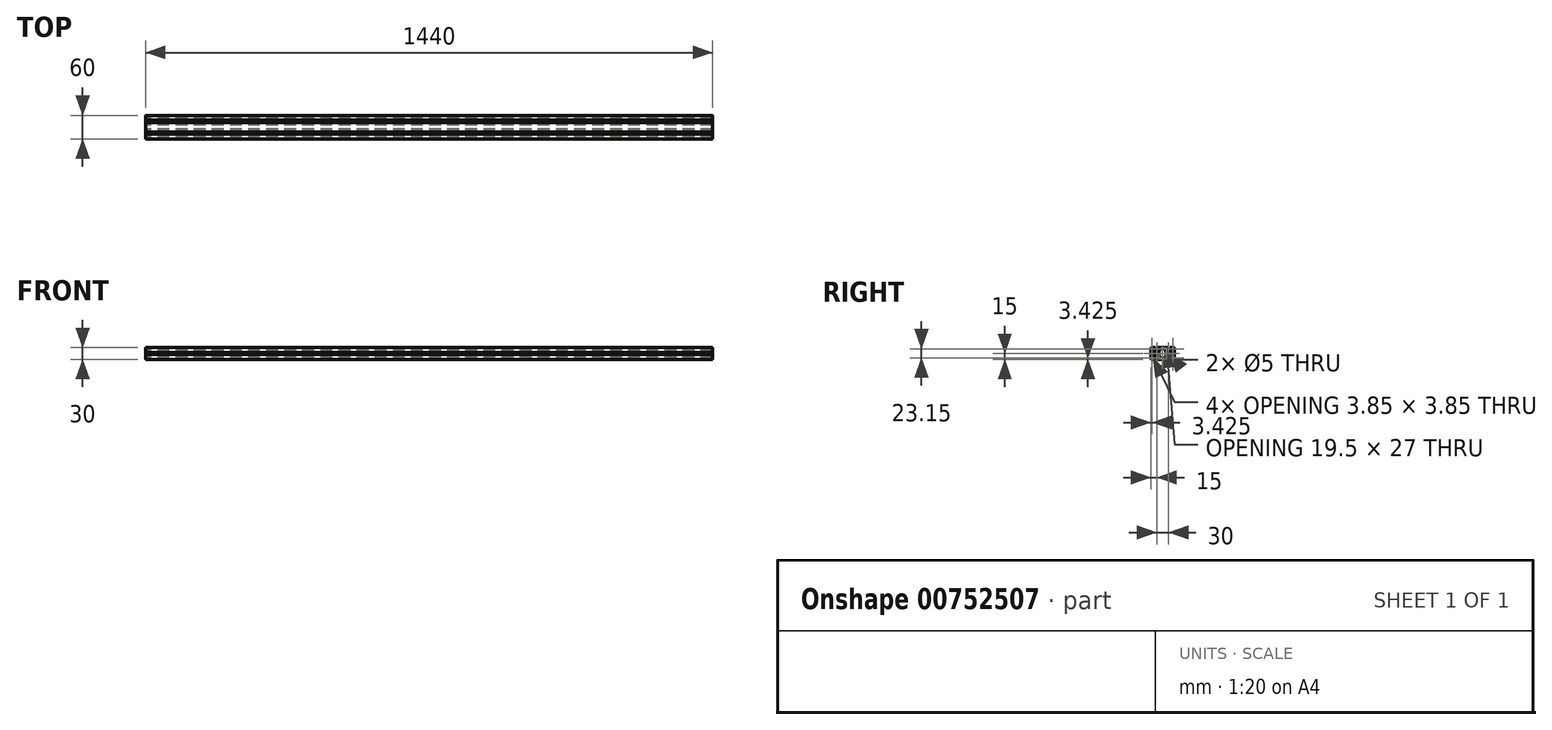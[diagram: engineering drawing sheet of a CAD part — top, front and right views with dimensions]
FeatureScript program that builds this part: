
annotation { "Feature Type Name" : "Feature", "Feature Type Description" : "" }
export const myFeature = defineFeature(function(context is Context, id is Id, definition is map)
    precondition{}
    {
        {
            var Q0;
            Q0=qCreatedBy(makeId("Right.planeOp"),FACE);
            var sketch = newSketch(context, id + "F0", { "sketchPlane" : qUnion([Q0])});
            skLineSegment(sketch, "E0.bottom", {"start": v(-12, 15) * mm, "end": v(-3.1, 15) * mm});
            skLineSegment(sketch, "E0.top", {"start": v(-12, -15) * mm, "end": v(-3.1, -15) * mm});
            skLineSegment(sketch, "E1", {"start": v(0, 31.7) * mm, "end": v(0, -24.01) * mm, "construction": true});
            skLineSegment(sketch, "E2", {"start": v(-29.71, 0) * mm, "end": v(21.95, 0) * mm, "construction": true});
            skLineSegment(sketch, "E3", {"start": v(-3.1, 15) * mm, "end": v(-3.1, 12.8) * mm});
            skLineSegment(sketch, "E4", {"start": v(-3.9, 12) * mm, "end": v(-5.6, 12) * mm});
            skLineSegment(sketch, "E5", {"start": v(-5.6, 12) * mm, "end": v(-5.6, 13.5) * mm});
            skLineSegment(sketch, "E6", {"start": v(-5.6, 13.5) * mm, "end": v(-8.15, 13.5) * mm});
            skLineSegment(sketch, "E7", {"start": v(-8.15, 13.5) * mm, "end": v(-8.15, 10.8) * mm});
            skLineSegment(sketch, "E8", {"start": v(-7.27, 8.68) * mm, "end": v(-4.72, 6.13) * mm});
            skLineSegment(sketch, "E9", {"start": v(-2.6, 5.25) * mm, "end": v(2.6, 5.25) * mm});
            skLineSegment(sketch, "E10", {"start": v(4.72, 6.13) * mm, "end": v(7.27, 8.68) * mm});
            skLineSegment(sketch, "E11", {"start": v(8.15, 10.8) * mm, "end": v(8.15, 13.5) * mm});
            skLineSegment(sketch, "E12", {"start": v(8.15, 13.5) * mm, "end": v(5.6, 13.5) * mm});
            skLineSegment(sketch, "E13", {"start": v(5.6, 13.5) * mm, "end": v(5.6, 12) * mm});
            skLineSegment(sketch, "E14", {"start": v(5.6, 12) * mm, "end": v(3.9, 12) * mm});
            skLineSegment(sketch, "E15", {"start": v(3.1, 12.8) * mm, "end": v(3.1, 15) * mm});
            skLineSegment(sketch, "E16.trimOffspring", {"start": v(3.1, 15) * mm, "end": v(12, 15) * mm});
            skLineSegment(sketch, "E17.bottom", {"start": v(-12, 13.5) * mm, "end": v(-9.65, 13.5) * mm});
            skLineSegment(sketch, "E17.top", {"start": v(-13.5, 9.65) * mm, "end": v(-9.65, 9.65) * mm});
            skLineSegment(sketch, "E17.left", {"start": v(-13.5, 12) * mm, "end": v(-13.5, 9.65) * mm});
            skLineSegment(sketch, "E17.right", {"start": v(-9.65, 13.5) * mm, "end": v(-9.65, 9.65) * mm});
            skPoint(sketch, "E18.visualSharp", {"position": v(-13.5, 13.5) * mm});
            skArc(sketch, "E18.filletArc", {"start": v(-12, 13.5) * mm, "mid": v(-13.06, 13.06) * mm, "end": v(-13.5, 12) * mm});
            skPoint(sketch, "E19.visualSharp", {"position": v(-14.85, 15) * mm});
            skArc(sketch, "E19.filletArc", {"start": v(-12, 15) * mm, "mid": v(-14.12, 14.12) * mm, "end": v(-15, 12) * mm});
            skPoint(sketch, "E20.visualSharp", {"position": v(-14.85, -15) * mm});
            skArc(sketch, "E20.filletArc", {"start": v(-15, -12) * mm, "mid": v(-14.12, -14.12) * mm, "end": v(-12, -15) * mm});
            skPoint(sketch, "E21.visualSharp", {"position": v(15.15, -15) * mm});
            skPoint(sketch, "E22.visualSharp", {"position": v(-8.15, 9.56) * mm});
            skArc(sketch, "E22.filletArc", {"start": v(-8.15, 10.8) * mm, "mid": v(-7.92, 9.66) * mm, "end": v(-7.27, 8.68) * mm});
            skPoint(sketch, "E23.visualSharp", {"position": v(-3.84, 5.25) * mm});
            skArc(sketch, "E23.filletArc", {"start": v(-4.72, 6.13) * mm, "mid": v(-3.74, 5.48) * mm, "end": v(-2.6, 5.25) * mm});
            skPoint(sketch, "E24.visualSharp", {"position": v(3.84, 5.25) * mm});
            skArc(sketch, "E24.filletArc", {"start": v(2.6, 5.25) * mm, "mid": v(3.74, 5.48) * mm, "end": v(4.72, 6.13) * mm});
            skPoint(sketch, "E25.visualSharp", {"position": v(8.15, 9.56) * mm});
            skArc(sketch, "E25.filletArc", {"start": v(7.27, 8.68) * mm, "mid": v(7.92, 9.66) * mm, "end": v(8.15, 10.8) * mm});
            skPoint(sketch, "E26.visualSharp", {"position": v(3.1, 12) * mm});
            skArc(sketch, "E26.filletArc", {"start": v(3.1, 12.8) * mm, "mid": v(3.33, 12.23) * mm, "end": v(3.9, 12) * mm});
            skPoint(sketch, "E27.visualSharp", {"position": v(-3.1, 12) * mm});
            skArc(sketch, "E27.filletArc", {"start": v(-3.9, 12) * mm, "mid": v(-3.33, 12.23) * mm, "end": v(-3.1, 12.8) * mm});
            skLineSegment(sketch, "E28.1.0", {"start": v(-5.25, -2.6) * mm, "end": v(-5.25, 2.6) * mm});
            skLineSegment(sketch, "E28.1.1", {"start": v(-12.8, 3.1) * mm, "end": v(-15, 3.1) * mm});
            skLineSegment(sketch, "E28.1.2", {"start": v(-6.13, 4.72) * mm, "end": v(-8.68, 7.27) * mm});
            skPoint(sketch, "E28.1.3", {"position": v(-12, -3.1) * mm});
            skLineSegment(sketch, "E28.1.4", {"start": v(-13.5, -5.6) * mm, "end": v(-13.5, -8.15) * mm});
            skPoint(sketch, "E28.1.5", {"position": v(-5.25, 3.84) * mm});
            skLineSegment(sketch, "E28.1.6", {"start": v(-13.5, -12) * mm, "end": v(-13.5, -9.65) * mm});
            skPoint(sketch, "E28.1.7", {"position": v(-5.25, -3.84) * mm});
            skLineSegment(sketch, "E28.1.8", {"start": v(-10.8, 8.15) * mm, "end": v(-13.5, 8.15) * mm});
            skLineSegment(sketch, "E28.1.9", {"start": v(-9.65, -13.5) * mm, "end": v(-9.65, -9.65) * mm});
            skLineSegment(sketch, "E28.1.10", {"start": v(-12, -13.5) * mm, "end": v(-9.65, -13.5) * mm});
            skLineSegment(sketch, "E28.1.11", {"start": v(-13.5, -8.15) * mm, "end": v(-10.8, -8.15) * mm});
            skLineSegment(sketch, "E28.1.12", {"start": v(-13.5, -9.65) * mm, "end": v(-9.65, -9.65) * mm});
            skPoint(sketch, "E28.1.13", {"position": v(-9.56, 8.15) * mm});
            skLineSegment(sketch, "E28.1.14", {"start": v(-8.68, -7.27) * mm, "end": v(-6.13, -4.72) * mm});
            skPoint(sketch, "E28.1.15", {"position": v(-12, 3.1) * mm});
            skPoint(sketch, "E28.1.16", {"position": v(-9.56, -8.15) * mm});
            skLineSegment(sketch, "E28.1.17", {"start": v(-15, -3.1) * mm, "end": v(-12.8, -3.1) * mm});
            skLineSegment(sketch, "E28.1.18", {"start": v(-13.5, 8.15) * mm, "end": v(-13.5, 5.6) * mm});
            skArc(sketch, "E28.1.19", {"start": v(-10.8, -8.15) * mm, "mid": v(-9.66, -7.92) * mm, "end": v(-8.68, -7.27) * mm});
            skArc(sketch, "E28.1.20", {"start": v(-6.13, -4.72) * mm, "mid": v(-5.48, -3.74) * mm, "end": v(-5.25, -2.6) * mm});
            skArc(sketch, "E28.1.21", {"start": v(-13.5, -12) * mm, "mid": v(-13.06, -13.06) * mm, "end": v(-12, -13.5) * mm});
            skArc(sketch, "E28.1.22", {"start": v(-8.68, 7.27) * mm, "mid": v(-9.66, 7.92) * mm, "end": v(-10.8, 8.15) * mm});
            skArc(sketch, "E28.1.23", {"start": v(-5.25, 2.6) * mm, "mid": v(-5.48, 3.74) * mm, "end": v(-6.13, 4.72) * mm});
            skLineSegment(sketch, "E28.1.24", {"start": v(-12, -5.6) * mm, "end": v(-13.5, -5.6) * mm});
            skLineSegment(sketch, "E28.1.25", {"start": v(-13.5, 5.6) * mm, "end": v(-12, 5.6) * mm});
            skLineSegment(sketch, "E28.1.26", {"start": v(-12, 5.6) * mm, "end": v(-12, 3.9) * mm});
            skLineSegment(sketch, "E28.1.27", {"start": v(-12, -3.9) * mm, "end": v(-12, -5.6) * mm});
            skArc(sketch, "E28.1.28", {"start": v(-12, -3.9) * mm, "mid": v(-12.23, -3.33) * mm, "end": v(-12.8, -3.1) * mm});
            skArc(sketch, "E28.1.29", {"start": v(-12.8, 3.1) * mm, "mid": v(-12.23, 3.33) * mm, "end": v(-12, 3.9) * mm});
            skLineSegment(sketch, "E28.2.0", {"start": v(2.6, -5.25) * mm, "end": v(-2.6, -5.25) * mm});
            skLineSegment(sketch, "E28.2.1", {"start": v(-3.1, -12.8) * mm, "end": v(-3.1, -15) * mm});
            skLineSegment(sketch, "E28.2.2", {"start": v(-4.72, -6.13) * mm, "end": v(-7.27, -8.68) * mm});
            skPoint(sketch, "E28.2.3", {"position": v(3.1, -12) * mm});
            skLineSegment(sketch, "E28.2.4", {"start": v(5.6, -13.5) * mm, "end": v(8.15, -13.5) * mm});
            skPoint(sketch, "E28.2.5", {"position": v(-3.84, -5.25) * mm});
            skPoint(sketch, "E28.2.7", {"position": v(3.84, -5.25) * mm});
            skLineSegment(sketch, "E28.2.8", {"start": v(-8.15, -10.8) * mm, "end": v(-8.15, -13.5) * mm});
            skLineSegment(sketch, "E28.2.11", {"start": v(8.15, -13.5) * mm, "end": v(8.15, -10.8) * mm});
            skLineSegment(sketch, "E28.2.12", {"start": v(9.65, -13.5) * mm, "end": v(9.65, -9.65) * mm});
            skPoint(sketch, "E28.2.13", {"position": v(-8.15, -9.56) * mm});
            skLineSegment(sketch, "E28.2.14", {"start": v(7.27, -8.68) * mm, "end": v(4.72, -6.13) * mm});
            skPoint(sketch, "E28.2.15", {"position": v(-3.1, -12) * mm});
            skPoint(sketch, "E28.2.16", {"position": v(8.15, -9.56) * mm});
            skLineSegment(sketch, "E28.2.17", {"start": v(3.1, -15) * mm, "end": v(3.1, -12.8) * mm});
            skLineSegment(sketch, "E28.2.18", {"start": v(-8.15, -13.5) * mm, "end": v(-5.6, -13.5) * mm});
            skArc(sketch, "E28.2.19", {"start": v(8.15, -10.8) * mm, "mid": v(7.92, -9.66) * mm, "end": v(7.27, -8.68) * mm});
            skArc(sketch, "E28.2.20", {"start": v(4.72, -6.13) * mm, "mid": v(3.74, -5.48) * mm, "end": v(2.6, -5.25) * mm});
            skArc(sketch, "E28.2.22", {"start": v(-7.27, -8.68) * mm, "mid": v(-7.92, -9.66) * mm, "end": v(-8.15, -10.8) * mm});
            skArc(sketch, "E28.2.23", {"start": v(-2.6, -5.25) * mm, "mid": v(-3.74, -5.48) * mm, "end": v(-4.72, -6.13) * mm});
            skLineSegment(sketch, "E28.2.24", {"start": v(5.6, -12) * mm, "end": v(5.6, -13.5) * mm});
            skLineSegment(sketch, "E28.2.25", {"start": v(-5.6, -13.5) * mm, "end": v(-5.6, -12) * mm});
            skLineSegment(sketch, "E28.2.26", {"start": v(-5.6, -12) * mm, "end": v(-3.9, -12) * mm});
            skLineSegment(sketch, "E28.2.27", {"start": v(3.9, -12) * mm, "end": v(5.6, -12) * mm});
            skArc(sketch, "E28.2.28", {"start": v(3.9, -12) * mm, "mid": v(3.33, -12.23) * mm, "end": v(3.1, -12.8) * mm});
            skArc(sketch, "E28.2.29", {"start": v(-3.1, -12.8) * mm, "mid": v(-3.33, -12.23) * mm, "end": v(-3.9, -12) * mm});
            skLineSegment(sketch, "E28.3.0", {"start": v(5.25, 2.6) * mm, "end": v(5.25, -2.6) * mm});
            skLineSegment(sketch, "E28.3.2", {"start": v(6.13, -4.72) * mm, "end": v(8.68, -7.27) * mm});
            skPoint(sketch, "E28.3.5", {"position": v(5.25, -3.84) * mm});
            skPoint(sketch, "E28.3.7", {"position": v(5.25, 3.84) * mm});
            skLineSegment(sketch, "E28.3.9", {"start": v(9.65, 13.5) * mm, "end": v(9.65, 9.56) * mm});
            skPoint(sketch, "E28.3.13", {"position": v(9.56, -8.15) * mm});
            skLineSegment(sketch, "E28.3.14", {"start": v(8.71, 7.3) * mm, "end": v(6.13, 4.72) * mm});
            skPoint(sketch, "E28.3.16", {"position": v(9.56, 8.15) * mm});
            skArc(sketch, "E28.3.20", {"start": v(6.13, 4.72) * mm, "mid": v(5.48, 3.74) * mm, "end": v(5.25, 2.6) * mm});
            skArc(sketch, "E28.3.23", {"start": v(5.25, -2.6) * mm, "mid": v(5.48, -3.74) * mm, "end": v(6.13, -4.72) * mm});
            skPoint(sketch, "E28.center", {"position": v(0, 0) * mm});
            skLineSegment(sketch, "E29.trimOffspring", {"start": v(-15, -3.1) * mm, "end": v(-15, -12) * mm});
            skLineSegment(sketch, "E30.trimOffspring", {"start": v(3.1, -15) * mm, "end": v(12, -15) * mm});
            skLineSegment(sketch, "E31", {"start": v(-15, 12) * mm, "end": v(-15, 3.1) * mm});
            skCircle(sketch, "E32", {"center": v(0, 0) * mm, "radius": 2.5 * mm});
            skPoint(sketch, "E33.1.0.0", {"position": v(26.9, -12) * mm});
            skPoint(sketch, "E33.1.0.1", {"position": v(45.65, 15) * mm});
            skPoint(sketch, "E33.1.0.3", {"position": v(30, 0) * mm});
            skPoint(sketch, "E33.1.0.4", {"position": v(35.25, -3.84) * mm});
            skPoint(sketch, "E33.1.0.5", {"position": v(33.1, 12) * mm});
            skPoint(sketch, "E33.1.0.7", {"position": v(35.25, 3.84) * mm});
            skPoint(sketch, "E33.1.0.8", {"position": v(42, 3.1) * mm});
            skPoint(sketch, "E33.1.0.9", {"position": v(33.1, -12) * mm});
            skLineSegment(sketch, "E33.1.0.10", {"start": v(30, 31.7) * mm, "end": v(30, -24.01) * mm, "construction": true});
            skLineSegment(sketch, "E33.1.0.11", {"start": v(0.29, 0) * mm, "end": v(51.95, 0) * mm, "construction": true});
            skPoint(sketch, "E33.1.0.13", {"position": v(42.5, -2.6) * mm});
            skPoint(sketch, "E33.1.0.15", {"position": v(45.15, -15) * mm});
            skPoint(sketch, "E33.1.0.16", {"position": v(24.75, 3.84) * mm});
            skPoint(sketch, "E33.1.0.17", {"position": v(24.75, -3.84) * mm});
            skPoint(sketch, "E33.1.0.18", {"position": v(26.16, 5.25) * mm});
            skLineSegment(sketch, "E33.1.0.20", {"start": v(32.6, -5.25) * mm, "end": v(27.4, -5.25) * mm});
            skArc(sketch, "E33.1.0.21", {"start": v(42, -15) * mm, "mid": v(44.12, -14.12) * mm, "end": v(45, -12) * mm});
            skPoint(sketch, "E33.1.0.22", {"position": v(33.84, 5.25) * mm});
            skArc(sketch, "E33.1.0.23", {"start": v(45, 12) * mm, "mid": v(44.12, 14.12) * mm, "end": v(42, 15) * mm});
            skCircle(sketch, "E33.1.0.24", {"center": v(30, 0) * mm, "radius": 2.5 * mm});
            skLineSegment(sketch, "E33.1.0.26", {"start": v(27.4, 5.25) * mm, "end": v(32.6, 5.25) * mm});
            skPoint(sketch, "E33.1.0.27", {"position": v(26.16, -5.25) * mm});
            skPoint(sketch, "E33.1.0.28", {"position": v(33.84, -5.25) * mm});
            skLineSegment(sketch, "E33.1.0.29", {"start": v(35.25, 2.6) * mm, "end": v(35.25, -2.6) * mm});
            skLineSegment(sketch, "E33.1.0.30", {"start": v(24.75, -2.6) * mm, "end": v(24.75, 2.6) * mm});
            skLineSegment(sketch, "E33.1.0.31", {"start": v(42.85, -3.1) * mm, "end": v(45, -3.1) * mm});
            skArc(sketch, "E33.1.0.32", {"start": v(24.75, 2.6) * mm, "mid": v(24.52, 3.74) * mm, "end": v(23.87, 4.72) * mm});
            skArc(sketch, "E33.1.0.34", {"start": v(35.25, -2.6) * mm, "mid": v(35.48, -3.74) * mm, "end": v(36.13, -4.72) * mm});
            skPoint(sketch, "E33.1.0.35", {"position": v(38.15, -9.56) * mm});
            skLineSegment(sketch, "E33.1.0.36", {"start": v(36.13, -4.72) * mm, "end": v(38.68, -7.27) * mm});
            skLineSegment(sketch, "E33.1.0.37", {"start": v(37.27, -8.68) * mm, "end": v(34.72, -6.13) * mm});
            skLineSegment(sketch, "E33.1.0.39", {"start": v(23.87, 4.72) * mm, "end": v(21.32, 7.27) * mm});
            skPoint(sketch, "E33.1.0.40", {"position": v(20.44, 8.15) * mm});
            skLineSegment(sketch, "E33.1.0.41", {"start": v(33.1, -15) * mm, "end": v(33.1, -12.8) * mm});
            skLineSegment(sketch, "E33.1.0.43", {"start": v(43.5, -5.6) * mm, "end": v(42.05, -5.6) * mm});
            skPoint(sketch, "E33.1.0.44", {"position": v(21.85, 9.56) * mm});
            skLineSegment(sketch, "E33.1.0.45", {"start": v(21.85, -13.5) * mm, "end": v(24.4, -13.5) * mm});
            skLineSegment(sketch, "E33.1.0.46", {"start": v(42.05, -5.6) * mm, "end": v(42.05, -3.9) * mm});
            skPoint(sketch, "E33.1.0.47", {"position": v(20.44, -8.15) * mm});
            skArc(sketch, "E33.1.0.52", {"start": v(42.85, -3.1) * mm, "mid": v(42.29, -3.33) * mm, "end": v(42.05, -3.9) * mm});
            skLineSegment(sketch, "E33.1.0.54", {"start": v(26.9, -12.8) * mm, "end": v(26.9, -15) * mm});
            skLineSegment(sketch, "E33.1.0.55", {"start": v(45, -3.1) * mm, "end": v(45, -12) * mm});
            skArc(sketch, "E33.1.0.56", {"start": v(27.4, -5.25) * mm, "mid": v(26.26, -5.48) * mm, "end": v(25.28, -6.13) * mm});
            skLineSegment(sketch, "E33.1.0.57", {"start": v(24.4, -13.5) * mm, "end": v(24.4, -12) * mm});
            skArc(sketch, "E33.1.0.59", {"start": v(25.28, 6.13) * mm, "mid": v(26.26, 5.48) * mm, "end": v(27.4, 5.25) * mm});
            skLineSegment(sketch, "E33.1.0.61", {"start": v(25.28, -6.13) * mm, "end": v(22.73, -8.68) * mm});
            skLineSegment(sketch, "E33.1.0.62", {"start": v(21.32, -7.27) * mm, "end": v(23.87, -4.72) * mm});
            skLineSegment(sketch, "E33.1.0.63", {"start": v(33.1, -15) * mm, "end": v(42, -15) * mm});
            skLineSegment(sketch, "E33.1.0.64", {"start": v(24.4, -12) * mm, "end": v(26.1, -12) * mm});
            skArc(sketch, "E33.1.0.65", {"start": v(32.6, 5.25) * mm, "mid": v(33.74, 5.48) * mm, "end": v(34.72, 6.13) * mm});
            skLineSegment(sketch, "E33.1.0.66", {"start": v(43.5, -8.15) * mm, "end": v(43.5, -5.6) * mm});
            skPoint(sketch, "E33.1.0.67", {"position": v(38.15, 9.56) * mm});
            skPoint(sketch, "E33.1.0.68", {"position": v(39.56, -8.15) * mm});
            skLineSegment(sketch, "E33.1.0.69", {"start": v(21.85, -10.8) * mm, "end": v(21.85, -13.5) * mm});
            skLineSegment(sketch, "E33.1.0.70", {"start": v(18, -15) * mm, "end": v(26.9, -15) * mm});
            skLineSegment(sketch, "E33.1.0.71", {"start": v(45, 12) * mm, "end": v(45, 3.1) * mm});
            skLineSegment(sketch, "E33.1.0.72", {"start": v(22.73, 8.68) * mm, "end": v(25.28, 6.13) * mm});
            skArc(sketch, "E33.1.0.73", {"start": v(36.13, 4.72) * mm, "mid": v(35.48, 3.74) * mm, "end": v(35.25, 2.6) * mm});
            skPoint(sketch, "E33.1.0.74", {"position": v(26.9, 12) * mm});
            skArc(sketch, "E33.1.0.75", {"start": v(33.9, -12) * mm, "mid": v(33.33, -12.23) * mm, "end": v(33.1, -12.8) * mm});
            skArc(sketch, "E33.1.0.76", {"start": v(23.87, -4.72) * mm, "mid": v(24.52, -3.74) * mm, "end": v(24.75, -2.6) * mm});
            skPoint(sketch, "E33.1.0.77", {"position": v(39.56, 8.15) * mm});
            skArc(sketch, "E33.1.0.78", {"start": v(26.9, -12.8) * mm, "mid": v(26.67, -12.23) * mm, "end": v(26.1, -12) * mm});
            skPoint(sketch, "E33.1.0.79", {"position": v(21.85, -9.56) * mm});
            skLineSegment(sketch, "E33.1.0.80", {"start": v(33.1, 15) * mm, "end": v(42, 15) * mm});
            skLineSegment(sketch, "E33.1.0.82", {"start": v(39.65, -13.5) * mm, "end": v(39.65, -9.65) * mm});
            skLineSegment(sketch, "E33.1.0.84", {"start": v(42, 5.6) * mm, "end": v(43.5, 5.6) * mm});
            skLineSegment(sketch, "E33.1.0.85", {"start": v(43.5, 5.6) * mm, "end": v(43.5, 8.15) * mm});
            skLineSegment(sketch, "E33.1.0.87", {"start": v(20.35, 13.5) * mm, "end": v(20.35, 9.65) * mm});
            skLineSegment(sketch, "E33.1.0.88", {"start": v(43.5, 12) * mm, "end": v(43.5, 9.65) * mm});
            skLineSegment(sketch, "E33.1.0.93", {"start": v(42, 3.9) * mm, "end": v(42, 5.6) * mm});
            skLineSegment(sketch, "E33.1.0.94", {"start": v(40.8, -8.15) * mm, "end": v(43.5, -8.15) * mm});
            skArc(sketch, "E33.1.0.95", {"start": v(38.15, -10.8) * mm, "mid": v(37.92, -9.66) * mm, "end": v(37.27, -8.68) * mm});
            skLineSegment(sketch, "E33.1.0.96", {"start": v(20.35, -13.5) * mm, "end": v(20.35, -9.65) * mm});
            skArc(sketch, "E33.1.0.97", {"start": v(42, 3.9) * mm, "mid": v(42.23, 3.33) * mm, "end": v(42.8, 3.1) * mm});
            skLineSegment(sketch, "E33.1.0.98", {"start": v(39.65, 13.5) * mm, "end": v(39.65, 9.65) * mm});
            skArc(sketch, "E33.1.0.99", {"start": v(34.72, -6.13) * mm, "mid": v(33.74, -5.48) * mm, "end": v(32.6, -5.25) * mm});
            skLineSegment(sketch, "E33.1.0.101", {"start": v(42, 13.5) * mm, "end": v(39.65, 13.5) * mm});
            skArc(sketch, "E33.1.0.102", {"start": v(42, -13.5) * mm, "mid": v(43.06, -13.06) * mm, "end": v(43.5, -12) * mm});
            skLineSegment(sketch, "E33.1.0.104", {"start": v(43.5, 8.15) * mm, "end": v(40.76, 8.15) * mm});
            skArc(sketch, "E33.1.0.105", {"start": v(22.73, -8.68) * mm, "mid": v(22.08, -9.66) * mm, "end": v(21.85, -10.8) * mm});
            skLineSegment(sketch, "E33.1.0.107", {"start": v(43.5, 9.65) * mm, "end": v(39.65, 9.65) * mm});
            skLineSegment(sketch, "E33.1.0.108", {"start": v(35.6, -13.5) * mm, "end": v(38.15, -13.5) * mm});
            skLineSegment(sketch, "E33.1.0.109", {"start": v(45, 3.1) * mm, "end": v(42.8, 3.1) * mm});
            skArc(sketch, "E33.1.0.110", {"start": v(21.85, 10.8) * mm, "mid": v(22.08, 9.66) * mm, "end": v(22.73, 8.68) * mm});
            skLineSegment(sketch, "E33.1.0.111", {"start": v(38.68, 7.27) * mm, "end": v(36.13, 4.72) * mm});
            skLineSegment(sketch, "E33.1.0.112", {"start": v(35.6, -12) * mm, "end": v(35.6, -13.5) * mm});
            skLineSegment(sketch, "E33.1.0.113", {"start": v(42, -13.5) * mm, "end": v(39.65, -13.5) * mm});
            skLineSegment(sketch, "E33.1.0.115", {"start": v(33.9, -12) * mm, "end": v(35.6, -12) * mm});
            skArc(sketch, "E33.1.0.117", {"start": v(37.27, 8.68) * mm, "mid": v(37.92, 9.66) * mm, "end": v(38.15, 10.8) * mm});
            skArc(sketch, "E33.1.0.118", {"start": v(40.76, 8.15) * mm, "mid": v(39.64, 7.91) * mm, "end": v(38.68, 7.27) * mm});
            skLineSegment(sketch, "E33.1.0.119", {"start": v(38.15, 10.8) * mm, "end": v(38.15, 13.5) * mm});
            skLineSegment(sketch, "E33.1.0.120", {"start": v(38.15, 13.5) * mm, "end": v(35.6, 13.5) * mm});
            skLineSegment(sketch, "E33.1.0.121", {"start": v(35.6, 13.5) * mm, "end": v(35.6, 12) * mm});
            skLineSegment(sketch, "E33.1.0.122", {"start": v(18, 15) * mm, "end": v(26.9, 15) * mm});
            skLineSegment(sketch, "E33.1.0.123", {"start": v(26.9, 15) * mm, "end": v(26.9, 12.8) * mm});
            skLineSegment(sketch, "E33.1.0.124", {"start": v(24.4, 12) * mm, "end": v(24.4, 13.5) * mm});
            skLineSegment(sketch, "E33.1.0.125", {"start": v(24.4, 13.5) * mm, "end": v(21.85, 13.5) * mm});
            skLineSegment(sketch, "E33.1.0.126", {"start": v(21.85, 13.5) * mm, "end": v(21.85, 10.8) * mm});
            skLineSegment(sketch, "E33.1.0.127", {"start": v(34.72, 6.13) * mm, "end": v(37.27, 8.68) * mm});
            skLineSegment(sketch, "E33.1.0.128", {"start": v(35.6, 12) * mm, "end": v(33.9, 12) * mm});
            skLineSegment(sketch, "E33.1.0.129", {"start": v(43.5, -9.65) * mm, "end": v(39.65, -9.65) * mm});
            skLineSegment(sketch, "E33.1.0.130", {"start": v(33.1, 12.8) * mm, "end": v(33.1, 15) * mm});
            skLineSegment(sketch, "E33.1.0.131", {"start": v(43.5, -12) * mm, "end": v(43.5, -9.65) * mm});
            skArc(sketch, "E33.1.0.133", {"start": v(43.5, 12) * mm, "mid": v(43.06, 13.06) * mm, "end": v(42, 13.5) * mm});
            skLineSegment(sketch, "E33.1.0.134", {"start": v(38.15, -13.5) * mm, "end": v(38.15, -10.8) * mm});
            skArc(sketch, "E33.1.0.136", {"start": v(38.68, -7.27) * mm, "mid": v(39.66, -7.92) * mm, "end": v(40.8, -8.15) * mm});
            skLineSegment(sketch, "E33.1.0.138", {"start": v(26.1, 12) * mm, "end": v(24.4, 12) * mm});
            skArc(sketch, "E33.1.0.139", {"start": v(33.1, 12.8) * mm, "mid": v(33.33, 12.23) * mm, "end": v(33.9, 12) * mm});
            skArc(sketch, "E33.1.0.140", {"start": v(26.1, 12) * mm, "mid": v(26.67, 12.23) * mm, "end": v(26.9, 12.8) * mm});
            skLineSegment(sketch, "E33.direction1", {"start": v(-14.85, -15) * mm, "end": v(15.15, -15) * mm, "construction": true});
            skLineSegment(sketch, "E34", {"start": v(9.65, 13.5) * mm, "end": v(20.35, 13.5) * mm});
            skArc(sketch, "E35", {"start": v(8.71, 7.3) * mm, "mid": v(9.4, 8.34) * mm, "end": v(9.65, 9.56) * mm});
            skArc(sketch, "E36", {"start": v(20.35, 9.65) * mm, "mid": v(20.6, 8.37) * mm, "end": v(21.32, 7.27) * mm});
            skArc(sketch, "E37", {"start": v(9.65, -9.65) * mm, "mid": v(9.4, -8.36) * mm, "end": v(8.68, -7.27) * mm});
            skArc(sketch, "E38", {"start": v(21.32, -7.27) * mm, "mid": v(20.6, -8.37) * mm, "end": v(20.35, -9.65) * mm});
            skLineSegment(sketch, "E39", {"start": v(12, -15) * mm, "end": v(18, -15) * mm});
            skLineSegment(sketch, "E40", {"start": v(12, 15) * mm, "end": v(18.49, 15) * mm});
            skLineSegment(sketch, "E41", {"start": v(9.65, -13.5) * mm, "end": v(20.35, -13.5) * mm});
            skSolve(sketch);
        }
        {
            var Q0;
            Q0=qSketchRegion(id+"F0",true);
            extrude(context, id + "F1", {"entities" : qUnion([Q0]), "depth" : 1440 * mm, "offsetDistance" : 25 * mm});
        }
    });
